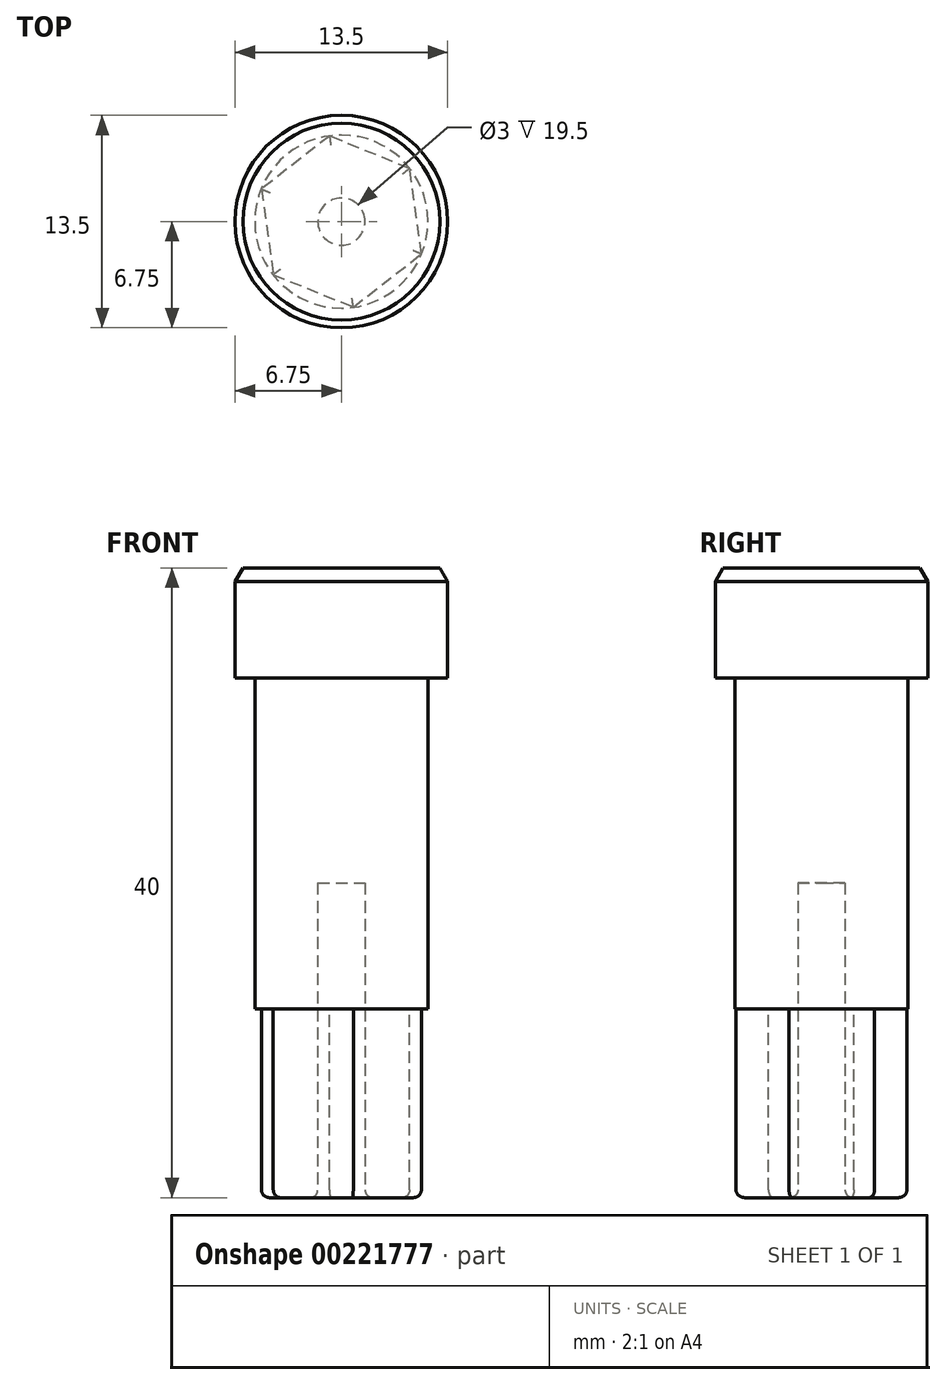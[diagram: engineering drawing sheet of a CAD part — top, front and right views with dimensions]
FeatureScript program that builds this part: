
annotation { "Feature Type Name" : "Feature", "Feature Type Description" : "" }
export const myFeature = defineFeature(function(context is Context, id is Id, definition is map)
    precondition{}
    {
        {
            var Q0;
            Q0=qCreatedBy(makeId("Top.planeOp"),FACE);
            var sketch = newSketch(context, id + "F0", { "sketchPlane" : qUnion([Q0])});
            skCircle(sketch, "E0", {"center": v(0, 0) * mm, "radius": 5.5 * mm});
            skSolve(sketch);
        }
        {
            var Q0;
            Q0 = qSketchRegion(id + "F0", true);
            extrude(context, id + "F1", {"entities" : qUnion([Q0]), "depth" : 21 * mm});
        }
        {
            var Q0;
            Q0=makeQuery(id+"F1.opExtrude","CAP_FACE",FACE,{"disambiguationData":[OSD([sQuery(id+"F0.wireOp",EDGE,"E0")])],"isStart":false});
            var sketch = newSketch(context, id + "F2", { "sketchPlane" : qUnion([Q0])});
            skCircle(sketch, "E1", {"center": v(0, 0) * mm, "radius": 6.75 * mm});
            skSolve(sketch);
        }
        {
            var Q0;
            Q0 = qSketchRegion(id + "F2", true);
            extrude(context, id + "F3", {"entities" : qUnion([Q0]), "operationType" : NewBodyOperationType.ADD, "depth" : 7 * mm});
        }
        {
            var Q0;
            Q0=makeQuery(id+"F1.opExtrude","CAP_FACE",FACE,{"disambiguationData":[OSD([sQuery(id+"F0.wireOp",EDGE,"E0")])],"isStart":true});
            var sketch = newSketch(context, id + "F4", { "sketchPlane" : qUnion([Q0])});
            skCircle(sketch, "E2.cCircle", {"center": v(0, 0) * mm, "radius": 4.75 * mm, "construction": true});
            skLineSegment(sketch, "E2.0", {"start": v(-4.33, 3.37) * mm, "end": v(0.75, 5.43) * mm});
            skLineSegment(sketch, "E2.1", {"start": v(0.75, 5.43) * mm, "end": v(5.08, 2.06) * mm});
            skLineSegment(sketch, "E2.2", {"start": v(5.08, 2.06) * mm, "end": v(4.33, -3.37) * mm});
            skLineSegment(sketch, "E2.3", {"start": v(4.33, -3.37) * mm, "end": v(-0.75, -5.43) * mm});
            skLineSegment(sketch, "E2.4", {"start": v(-0.75, -5.43) * mm, "end": v(-5.08, -2.06) * mm});
            skLineSegment(sketch, "E2.5", {"start": v(-5.08, -2.06) * mm, "end": v(-4.33, 3.37) * mm});
            skPoint(sketch, "E2.0.midPoint", {"position": v(-1.79, 4.4) * mm});
            skSolve(sketch);
        }
        {
            var Q0;
            Q0 = qSketchRegion(id + "F4", true);
            extrude(context, id + "F5", {"entities" : qUnion([Q0]), "operationType" : NewBodyOperationType.ADD, "depth" : 12 * mm});
        }
        {
            var Q0;
            Q0=makeQuery(id+"F5.opExtrude","CAP_FACE",FACE,{"disambiguationData":[OSD([sQuery(id+"F4.wireOp",EDGE,"E2.0"),sQuery(id+"F4.wireOp",EDGE,"E2.1"),sQuery(id+"F4.wireOp",EDGE,"E2.2"),sQuery(id+"F4.wireOp",EDGE,"E2.3"),sQuery(id+"F4.wireOp",EDGE,"E2.4"),sQuery(id+"F4.wireOp",EDGE,"E2.5")])],"isStart":false});
            var sketch = newSketch(context, id + "F6", { "sketchPlane" : qUnion([Q0])});
            skCircle(sketch, "E3", {"center": v(0, 0) * mm, "radius": 1.5 * mm});
            skSolve(sketch);
        }
        {
            var Q0;
            Q0 = qSketchRegion(id + "F6", true);
            extrude(context, id + "F7", {"entities" : qUnion([Q0]), "operationType" : NewBodyOperationType.REMOVE, "oppositeDirection" : true, "depth" : 20 * mm});
        }
        {
            var Q0;
            Q0=makeQuery(id+"F5.opExtrude","CAP_FACE",FACE,{"disambiguationData":[OSD([sQuery(id+"F4.wireOp",EDGE,"E2.0"),sQuery(id+"F4.wireOp",EDGE,"E2.1"),sQuery(id+"F4.wireOp",EDGE,"E2.2"),sQuery(id+"F4.wireOp",EDGE,"E2.3"),sQuery(id+"F4.wireOp",EDGE,"E2.4"),sQuery(id+"F4.wireOp",EDGE,"E2.5")])],"isStart":false});
            fillet(context, id + "F8", {"entities" : qUnion([Q0]), "radius" : .5 * mm, "tangentPropagation" : true, "allowEdgeOverflow" : false});
        }
        {
            var Q0;
            Q0=makeQuery(id+"F3.opExtrude","CAP_FACE",FACE,{"disambiguationData":[OSD([sQuery(id+"F2.wireOp",EDGE,"E1")])],"isStart":false});
            chamfer(context, id + "F9", {"entities" : qUnion([Q0]), "chamferType" : ChamferType.OFFSET_ANGLE, "width" : .5 * mm, "oppositeDirection" : false, "angle" : 60 * degree, "tangentPropagation" : true});
        }
    });
